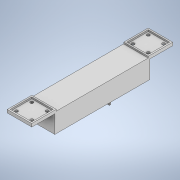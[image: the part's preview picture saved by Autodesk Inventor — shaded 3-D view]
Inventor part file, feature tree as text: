
AUTODESK INVENTOR PART (.ipt)
format: ipt  version: 2020 (Build 240168000, 168)  size: 271,872 bytes
history: native  units: in
note: dims shown in document units (in); Inventor stores cm internally (conversion verified against a paired STEP export)
features: extrude x11, sketch x11, mirror x3
ambient origin geometry x8: Origin, YZ Plane, XZ Plane, XY Plane, X Axis, Y Axis, Z Axis, Center Point
bodies: Solid1 (feature_tree)
feature tree (25):
  extrude  "Extrusion1"  Depth=10.8661in
  extrude  "Extrusion2"  Depth=0.1181in
  mirror  "Mirror1"
  extrude  "Extrusion3"  Depth=0.1181in
  extrude  "Extrusion4"  Depth=0.1181in
  extrude  "Extrusion5"  Depth=0.1181in
  extrude  "Extrusion6"  Depth=0.1181in
  mirror  "Mirror2"
  extrude  "Extrusion7"  Depth=0.1575in
  mirror  "Mirror3"
  extrude  "Extrusion8"  Depth=0.1575in
  extrude  "Extrusion9"  Depth=0.1575in
  extrude  "Extrusion10"  Depth=0.2362in
  extrude  "Extrusion11"  Depth=0.2362in
  sketch  "Sketch1"  dims[d0=1.8898in d1=10.8661in]
  sketch  "Sketch2"  dims[d2=0.1181in d3=0.0in d4=0.1181in]
  sketch  "Sketch3"  dims[d5=1.8898in d6=0.1181in]
  sketch  "Sketch4"  dims[d7=0.1181in d8=0.1181in]
  sketch  "Sketch5"  dims[d9=0.1181in d10=0.0in d11=0.1181in]
  sketch  "Sketch6"  dims[d12=0.1181in d13=0.1181in]
  sketch  "Sketch7"  dims[d14=1.378in d15=0.0in d16=0.1575in]
  sketch  "Sketch8"  dims[d17=0.315in d18=0.0in d19=0.1575in]
  sketch  "Sketch9"  dims[d20=0.1575in d21=0.0in d22=0.1575in]
  sketch  "Sketch10"  dims[d23=0.1575in d24=0.0in d25=0.2362in]
  sketch  "Sketch11"  dims[d26=0.2362in d27=0.2362in d28=0.2362in d29=0.1575in d30=0.0in d31=0.1181in d32=1.6654in d33=0.0in d34=0.315in d35=0.315in d36=0.315in d37=0.315in d38=0.1181in d39=0.0in d40=0.2362in d41=0.2362in d42=0.2362in d43=0.2362in d44=0.0787in d45=0.0in d46=0.9843in d47=0.1575in d48=0.1575in d49=0.1575in d50=0.1575in d51=0.3937in d52=0.0in]
